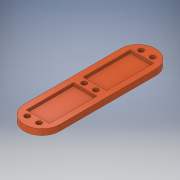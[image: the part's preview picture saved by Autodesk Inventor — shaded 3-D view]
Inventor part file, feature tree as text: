
AUTODESK INVENTOR PART (.ipt)
format: ipt  version: 2017 (Build 210142000, 142)  size: 156,160 bytes
history: native  units: mm
features: extrude x3, sketch x3, fillet x2
ambient origin geometry x8: Origin, YZ Plane, XZ Plane, XY Plane, X Axis, Y Axis, Z Axis, Center Point
bodies: Solid1 (feature_tree)
feature tree (8):
  extrude  "Extrusion1"  Depth=30.0mm
  extrude  "Extrusion2"  TaperAngle=0.0deg  [1 undecoded]
  extrude  "Extrusion4"  Depth=20.0mm
  fillet  "Fillet1"  Radius=40.5mm
  fillet  "Fillet2"  Radius=11.5mm
  sketch  "Sketch1"  dims[d0=30.0mm d1=112.0mm]
  sketch  "Sketch2"  dims[d2=5.0mm d3=0.0mm]
  sketch  "Sketch3"  dims[d4=5.0mm d5=20.0mm d6=40.5mm d7=11.5mm d8=2.5mm d9=0.0mm d13=4.0mm d14=4.0mm d15=2.75mm d16=2.75mm d17=4.5mm d18=2.5mm d19=0.0mm]
note: 1 required parameter value undecoded (feature->parameter linkage not recoverable at this tier; creation-order binding heuristic only, values carry confidence <= 0.55)
